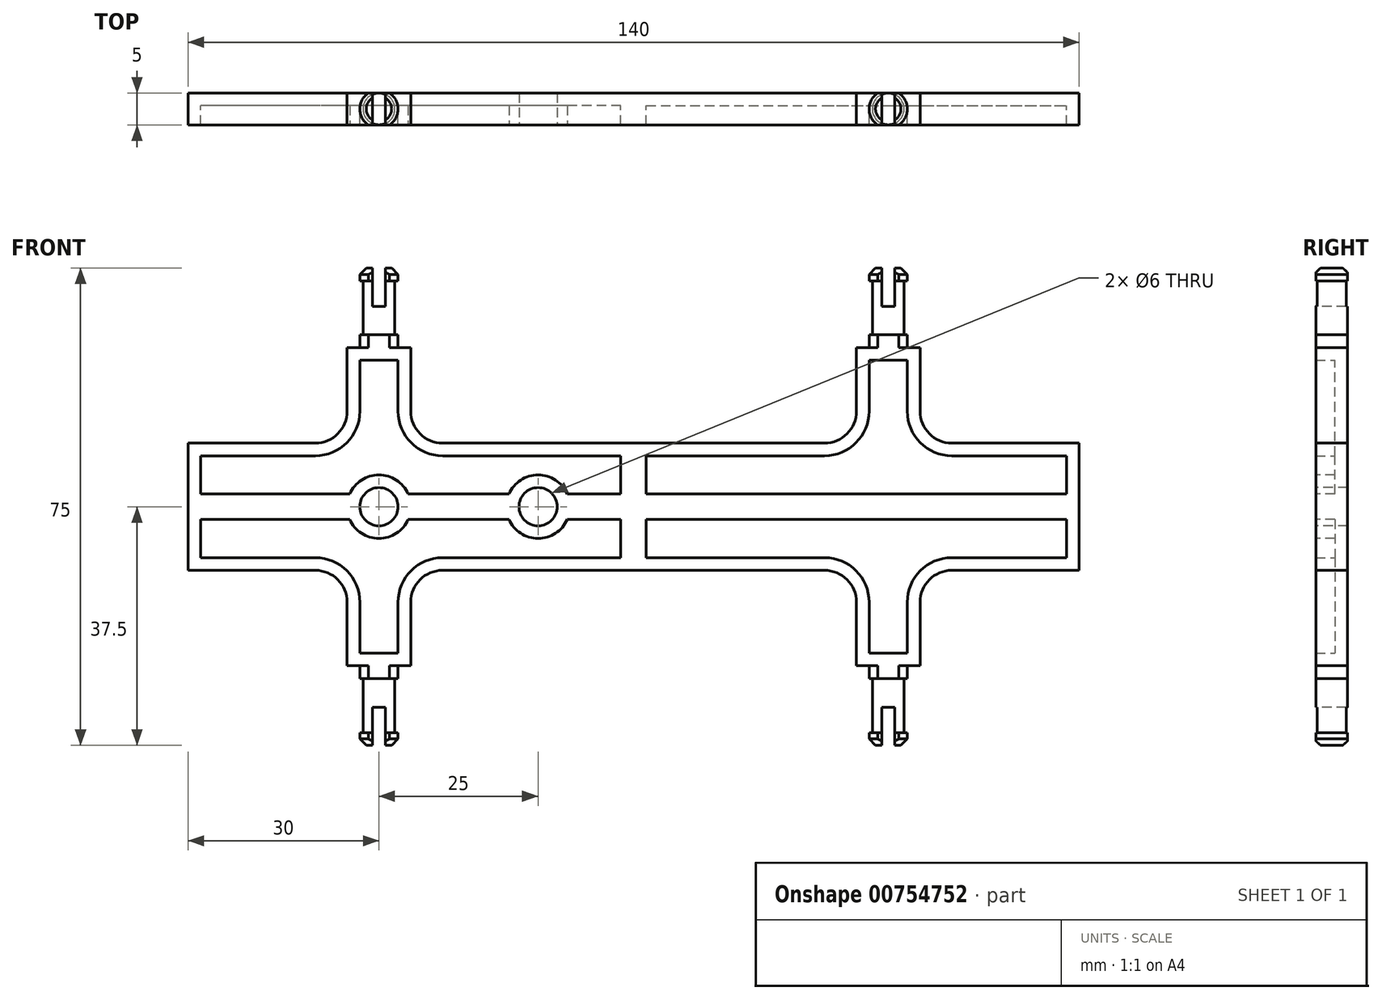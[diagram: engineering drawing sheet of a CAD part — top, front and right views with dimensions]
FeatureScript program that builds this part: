
annotation { "Feature Type Name" : "Feature", "Feature Type Description" : "" }
export const myFeature = defineFeature(function(context is Context, id is Id, definition is map)
    precondition{}
    {
        {
            var Q0;
            Q0=qCreatedBy(makeId("Front.planeOp"),FACE);
            var sketch = newSketch(context, id + "F0", { "sketchPlane" : qUnion([Q0])});
            skLineSegment(sketch, "E0.bottom", {"start": v(0, 0) * mm, "end": v(70, 0) * mm});
            skLineSegment(sketch, "E0.top", {"start": v(0, 10) * mm, "end": v(30, 10) * mm});
            skLineSegment(sketch, "E0.left", {"start": v(0, 0) * mm, "end": v(0, 10) * mm});
            skLineSegment(sketch, "E0.right", {"start": v(70, 0) * mm, "end": v(70, 10) * mm});
            skLineSegment(sketch, "E1.top", {"start": v(35, 25) * mm, "end": v(45, 25) * mm});
            skLineSegment(sketch, "E1.left", {"start": v(35, 15) * mm, "end": v(35, 25) * mm});
            skLineSegment(sketch, "E1.right", {"start": v(45, 15) * mm, "end": v(45, 25) * mm});
            skLineSegment(sketch, "E2.trimOffspring", {"start": v(50, 10) * mm, "end": v(70, 10) * mm});
            skPoint(sketch, "E3.visualSharp", {"position": v(35, 10) * mm});
            skArc(sketch, "E3.filletArc", {"start": v(30, 10) * mm, "mid": v(33.54, 11.46) * mm, "end": v(35, 15) * mm});
            skPoint(sketch, "E4.visualSharp", {"position": v(45, 10) * mm});
            skArc(sketch, "E4.filletArc", {"start": v(45, 15) * mm, "mid": v(46.46, 11.46) * mm, "end": v(50, 10) * mm});
            skSolve(sketch);
        }
        {
            var Q0;
            Q0 = qSketchRegion(id + "F0", true);
            extrude(context, id + "F1", {"entities" : qUnion([Q0]), "depth" : 5 * mm, "offsetDistance" : 25 * mm, "symmetric" : true});
        }
        {
            var Q0;
            Q0=makeQuery(id+"F1.opExtrude","CAP_FACE",FACE,{"disambiguationData":[OSD([sQuery(id+"F0.wireOp",EDGE,"E0.bottom"),sQuery(id+"F0.wireOp",EDGE,"E0.top"),sQuery(id+"F0.wireOp",EDGE,"E0.left"),sQuery(id+"F0.wireOp",EDGE,"E0.right"),sQuery(id+"F0.wireOp",EDGE,"E1.top"),sQuery(id+"F0.wireOp",EDGE,"E1.left"),sQuery(id+"F0.wireOp",EDGE,"E1.right"),sQuery(id+"F0.wireOp",EDGE,"E2.trimOffspring"),sQuery(id+"F0.wireOp",EDGE,"E3.filletArc"),sQuery(id+"F0.wireOp",EDGE,"E4.filletArc")])],"isStart":false});
            shell(context, id + "F2", {"entities" : qUnion([Q0]), "thickness" : 2 * mm});
        }
        {
            var Q0;
            Q0=qCreatedBy(makeId("Front.planeOp"),FACE);
            var sketch = newSketch(context, id + "F3", { "sketchPlane" : qUnion([Q0])});
            skLineSegment(sketch, "E5", {"start": v(40, 25) * mm, "end": v(40, 37.5) * mm});
            skLineSegment(sketch, "E6", {"start": v(40, 37.5) * mm, "end": v(37, 37.5) * mm});
            skLineSegment(sketch, "E7", {"start": v(37, 37.5) * mm, "end": v(37, 35.5) * mm});
            skLineSegment(sketch, "E8", {"start": v(37, 35.5) * mm, "end": v(37.5, 35.5) * mm});
            skLineSegment(sketch, "E9", {"start": v(37.5, 35.5) * mm, "end": v(37.5, 27) * mm});
            skLineSegment(sketch, "E10", {"start": v(37.5, 27) * mm, "end": v(37, 27) * mm});
            skLineSegment(sketch, "E11", {"start": v(37, 27) * mm, "end": v(37, 25) * mm});
            skLineSegment(sketch, "E12", {"start": v(37, 25) * mm, "end": v(40, 25) * mm});
            skSolve(sketch);
        }
        {
            var Q0;
            Q0=makeQuery(id+"F3.imprint","IMPRINT",FACE,{"disambiguationData":[TD([[makeQuery(id+"F3.imprint","IMPRINT",EDGE,{"derivedFrom":sQuery(id+"F3.wireOp",EDGE,"E5")}),1.0]])]});
            var Q1;
            Q1=sQuery(id+"F3.wireOp",EDGE,"E5");
            revolve(context, id + "F4", {"operationType" : NewBodyOperationType.ADD, "surfaceOperationType" : NewSurfaceOperationType.NEW, "entities" : qUnion([Q0]), "axis" : qUnion([Q1]), "revolveType" : RevolveType.FULL});
        }
        {
            var Q0;
            Q0=makeQuery(id+"F4.opRevolve","SWEPT_EDGE",EDGE,{"disambiguationData":[OSD([sQuery(id+"F3.wireOp",EDGE,"E6"),sQuery(id+"F3.wireOp",EDGE,"E7")])]});
            chamfer(context, id + "F5", {"entities" : qUnion([Q0]), "width" : 1 * mm, "tangentPropagation" : true});
        }
        {
            var Q0;
            Q0=makeQuery(id+"F4.opRevolve","SWEPT_FACE",FACE,{"disambiguationData":[OSD([sQuery(id+"F3.wireOp",EDGE,"E6")])]});
            var sketch = newSketch(context, id + "F6", { "sketchPlane" : qUnion([Q0])});
            skLineSegment(sketch, "E13.bottom", {"start": v(-2.76, 2.5) * mm, "end": v(75.35, 2.5) * mm});
            skLineSegment(sketch, "E13.top", {"start": v(-2.76, -2.5) * mm, "end": v(75.35, -2.5) * mm});
            skLineSegment(sketch, "E13.left", {"start": v(-2.76, 2.5) * mm, "end": v(-2.76, -2.5) * mm});
            skLineSegment(sketch, "E13.right", {"start": v(75.35, 2.5) * mm, "end": v(75.35, -2.5) * mm});
            skSolve(sketch);
        }
        {
            var Q0;
            Q0 = qSketchRegion(id + "F6", true);
            extrude(context, id + "F7", {"entities" : qUnion([Q0]), "operationType" : NewBodyOperationType.INTERSECT, "endBound" : BoundingType.THROUGH_ALL, "oppositeDirection" : true, "depth" : 25 * mm, "offsetDistance" : 25 * mm});
        }
        {
            var Q0;
            Q0=makeQuery(id+"F4.opRevolve","SWEPT_FACE",FACE,{"disambiguationData":[OSD([sQuery(id+"F3.wireOp",EDGE,"E6")])]});
            var sketch = newSketch(context, id + "F8", { "sketchPlane" : qUnion([Q0])});
            skLineSegment(sketch, "E14.bottom", {"start": v(39, 7.26) * mm, "end": v(41, 7.26) * mm});
            skLineSegment(sketch, "E14.top", {"start": v(39, -8.86) * mm, "end": v(41, -8.86) * mm});
            skLineSegment(sketch, "E14.left", {"start": v(39, 7.26) * mm, "end": v(39, -8.86) * mm});
            skLineSegment(sketch, "E14.right", {"start": v(41, 7.26) * mm, "end": v(41, -8.86) * mm});
            skSolve(sketch);
        }
        {
            var Q0;
            Q0 = qSketchRegion(id + "F8", true);
            extrude(context, id + "F9", {"entities" : qUnion([Q0]), "operationType" : NewBodyOperationType.REMOVE, "oppositeDirection" : true, "depth" : 6 * mm, "offsetDistance" : 25 * mm});
        }
        {
            var Q0;
            Q0=makeQuery(id+"F1.opExtrude","SWEPT_BODY",BODY,{"disambiguationData":[OSD([sQuery(id+"F0.wireOp",EDGE,"E0.bottom"),sQuery(id+"F0.wireOp",EDGE,"E0.top"),sQuery(id+"F0.wireOp",EDGE,"E0.left"),sQuery(id+"F0.wireOp",EDGE,"E0.right"),sQuery(id+"F0.wireOp",EDGE,"E1.top"),sQuery(id+"F0.wireOp",EDGE,"E1.left"),sQuery(id+"F0.wireOp",EDGE,"E1.right"),sQuery(id+"F0.wireOp",EDGE,"E2.trimOffspring"),sQuery(id+"F0.wireOp",EDGE,"E3.filletArc"),sQuery(id+"F0.wireOp",EDGE,"E4.filletArc")])]});
            var Q1;
            Q1=qCreatedBy(makeId("Top.planeOp"),FACE);
            mirror(context, id + "F10", {"operationType" : NewBodyOperationType.ADD, "entities" : qUnion([Q0]), "mirrorPlane" : qUnion([Q1])});
        }
        {
            var Q0;
            Q0=makeQuery(id+"F1.opExtrude","SWEPT_BODY",BODY,{"disambiguationData":[OSD([sQuery(id+"F0.wireOp",EDGE,"E0.bottom"),sQuery(id+"F0.wireOp",EDGE,"E0.top"),sQuery(id+"F0.wireOp",EDGE,"E0.left"),sQuery(id+"F0.wireOp",EDGE,"E0.right"),sQuery(id+"F0.wireOp",EDGE,"E1.top"),sQuery(id+"F0.wireOp",EDGE,"E1.left"),sQuery(id+"F0.wireOp",EDGE,"E1.right"),sQuery(id+"F0.wireOp",EDGE,"E2.trimOffspring"),sQuery(id+"F0.wireOp",EDGE,"E3.filletArc"),sQuery(id+"F0.wireOp",EDGE,"E4.filletArc")])]});
            var Q1;
            Q1=qCreatedBy(makeId("Right.planeOp"),FACE);
            mirror(context, id + "F11", {"operationType" : NewBodyOperationType.ADD, "entities" : qUnion([Q0]), "mirrorPlane" : qUnion([Q1])});
        }
        {
            var Q0;
            {var subQ0=makeQuery(id+"F7.boolean.opBoolean","MERGE",FACE,{"derivedFrom":[makeQuery(id+"F1.opExtrude","CAP_FACE",FACE,{"disambiguationData":[OSD([sQuery(id+"F0.wireOp",EDGE,"E0.bottom"),sQuery(id+"F0.wireOp",EDGE,"E0.top"),sQuery(id+"F0.wireOp",EDGE,"E0.left"),sQuery(id+"F0.wireOp",EDGE,"E0.right"),sQuery(id+"F0.wireOp",EDGE,"E1.top"),sQuery(id+"F0.wireOp",EDGE,"E1.left"),sQuery(id+"F0.wireOp",EDGE,"E1.right"),sQuery(id+"F0.wireOp",EDGE,"E2.trimOffspring"),sQuery(id+"F0.wireOp",EDGE,"E3.filletArc"),sQuery(id+"F0.wireOp",EDGE,"E4.filletArc")])],"isStart":false}),makeQuery(id+"F7.boolean.toolComplement.opBoolean","COPY",FACE,{"derivedFrom":makeQuery(id+"F7.opExtrude","SWEPT_FACE",FACE,{"disambiguationData":[OSD([sQuery(id+"F6.wireOp",EDGE,"E13.top")])]})})]});var subQ1=makeQuery(id+"F10.boolean.opBoolean","MERGE",FACE,{"derivedFrom":[subQ0,makeQuery(id+"F10.opPattern","COPY",FACE,{"derivedFrom":subQ0,"instanceName":"1"})]});Q0=makeQuery(id+"F11.boolean.opBoolean","MERGE",FACE,{"derivedFrom":[subQ1,makeQuery(id+"F11.opPattern","COPY",FACE,{"derivedFrom":subQ1,"instanceName":"1"})]});}
            var sketch = newSketch(context, id + "F12", { "sketchPlane" : qUnion([Q0])});
            skCircle(sketch, "E15", {"center": v(-40, 0) * mm, "radius": 5 * mm});
            skCircle(sketch, "E16", {"center": v(-15, 0) * mm, "radius": 5 * mm});
            skSolve(sketch);
        }
        {
            var Q0;
            Q0 = qSketchRegion(id + "F12", true);
            extrude(context, id + "F13", {"entities" : qUnion([Q0]), "operationType" : NewBodyOperationType.ADD, "endBound" : BoundingType.UP_TO_NEXT, "oppositeDirection" : true, "depth" : 25 * mm, "offsetDistance" : 25 * mm});
        }
        {
            var Q0;
            {var subQ0=makeQuery(id+"F7.boolean.opBoolean","MERGE",FACE,{"derivedFrom":[makeQuery(id+"F1.opExtrude","CAP_FACE",FACE,{"disambiguationData":[OSD([sQuery(id+"F0.wireOp",EDGE,"E0.bottom"),sQuery(id+"F0.wireOp",EDGE,"E0.top"),sQuery(id+"F0.wireOp",EDGE,"E0.left"),sQuery(id+"F0.wireOp",EDGE,"E0.right"),sQuery(id+"F0.wireOp",EDGE,"E1.top"),sQuery(id+"F0.wireOp",EDGE,"E1.left"),sQuery(id+"F0.wireOp",EDGE,"E1.right"),sQuery(id+"F0.wireOp",EDGE,"E2.trimOffspring"),sQuery(id+"F0.wireOp",EDGE,"E3.filletArc"),sQuery(id+"F0.wireOp",EDGE,"E4.filletArc")])],"isStart":false}),makeQuery(id+"F7.boolean.toolComplement.opBoolean","COPY",FACE,{"derivedFrom":makeQuery(id+"F7.opExtrude","SWEPT_FACE",FACE,{"disambiguationData":[OSD([sQuery(id+"F6.wireOp",EDGE,"E13.top")])]})})]});var subQ1=makeQuery(id+"F10.boolean.opBoolean","MERGE",FACE,{"derivedFrom":[subQ0,makeQuery(id+"F10.opPattern","COPY",FACE,{"derivedFrom":subQ0,"instanceName":"1"})]});Q0=makeQuery(id+"F13.boolean.opBoolean","MERGE",FACE,{"derivedFrom":[makeQuery(id+"F11.boolean.opBoolean","MERGE",FACE,{"derivedFrom":[subQ1,makeQuery(id+"F11.opPattern","COPY",FACE,{"derivedFrom":subQ1,"instanceName":"1"})]}),makeQuery(id+"F13.opExtrude","CAP_FACE",FACE,{"disambiguationData":[OSD([sQuery(id+"F12.wireOp",EDGE,"E15")])],"isStart":true}),makeQuery(id+"F13.opExtrude","CAP_FACE",FACE,{"disambiguationData":[OSD([sQuery(id+"F12.wireOp",EDGE,"E16")])],"isStart":true})]});}
            var sketch = newSketch(context, id + "F14", { "sketchPlane" : qUnion([Q0])});
            skPoint(sketch, "E17", {"position": v(-40, 0) * mm});
            skPoint(sketch, "E18", {"position": v(-15, 0) * mm});
            skSolve(sketch);
        }
        {
            var Q0;
            Q0=sQuery(id+"F14.wireOp",VERTEX,"E17");
            var Q1;
            Q1=sQuery(id+"F14.wireOp",VERTEX,"E18");
            var Q2;
            Q2=makeQuery(id+"F1.opExtrude","SWEPT_BODY",BODY,{"disambiguationData":[OSD([sQuery(id+"F0.wireOp",EDGE,"E0.bottom"),sQuery(id+"F0.wireOp",EDGE,"E0.top"),sQuery(id+"F0.wireOp",EDGE,"E0.left"),sQuery(id+"F0.wireOp",EDGE,"E0.right"),sQuery(id+"F0.wireOp",EDGE,"E1.top"),sQuery(id+"F0.wireOp",EDGE,"E1.left"),sQuery(id+"F0.wireOp",EDGE,"E1.right"),sQuery(id+"F0.wireOp",EDGE,"E2.trimOffspring"),sQuery(id+"F0.wireOp",EDGE,"E3.filletArc"),sQuery(id+"F0.wireOp",EDGE,"E4.filletArc")])]});
            hole(context, id + "F15", {"style" : HoleStyle.SIMPLE, "endStyle" : HoleEndStyle.THROUGH, "holeDiameter" : 6 * mm, "majorDiameter" : 5 * mm, "isTappedThrough" : true, "tappedDepth" : 12 * mm, "tapClearance" : 3, "locations" : qUnion([Q0, Q1]), "scope" : qUnion([Q2])});
        }
    });
